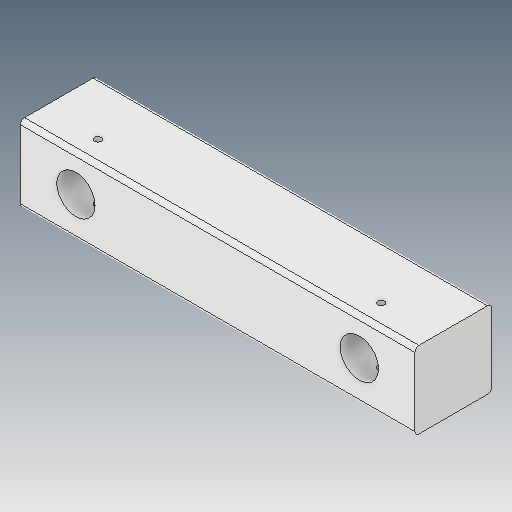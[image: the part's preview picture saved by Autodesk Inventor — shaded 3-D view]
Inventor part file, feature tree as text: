
AUTODESK INVENTOR PART (.ipt)
format: ipt  version: 2023.5 (Build 275446000, 446)  size: 106,496 bytes
history: native  units: in
note: dims shown in document units (in); Inventor stores cm internally (conversion verified against a paired STEP export)
features: fillet x1
ambient origin geometry x8: Origin, YZ Plane, XZ Plane, XY Plane, X Axis, Y Axis, Z Axis, Center Point
bodies: Solid1 (feature_tree)
feature tree (1):
  fillet  "Fillet1"  [1 undecoded]
note: 1 required parameter value undecoded (feature->parameter linkage not recoverable at this tier; creation-order binding heuristic only, values carry confidence <= 0.55)
